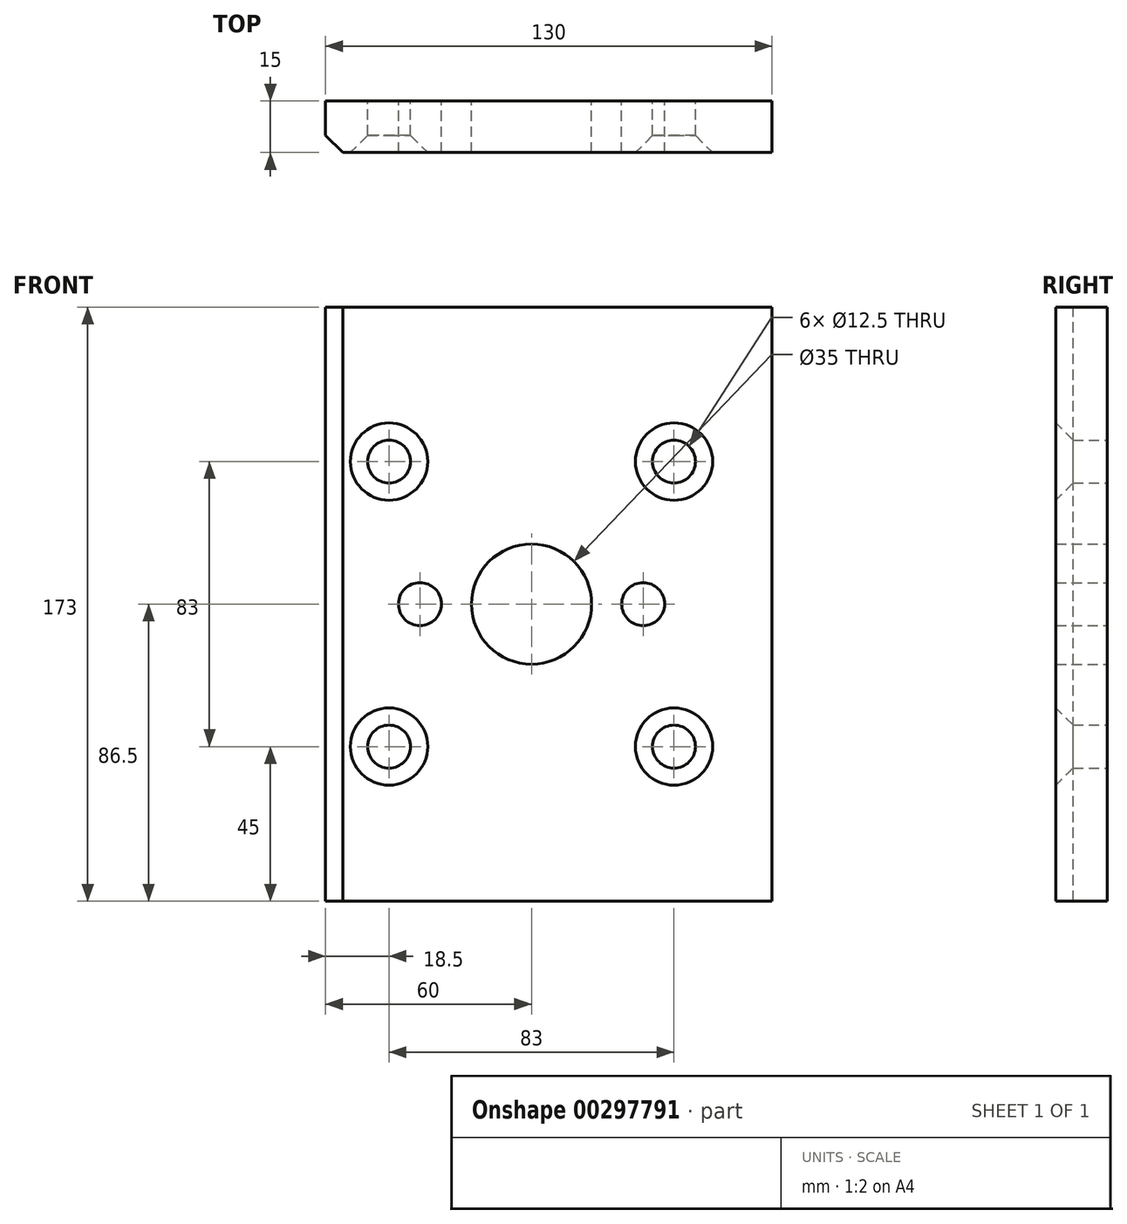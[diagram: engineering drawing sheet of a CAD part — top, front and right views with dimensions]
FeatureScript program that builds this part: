
annotation { "Feature Type Name" : "Feature", "Feature Type Description" : "" }
export const myFeature = defineFeature(function(context is Context, id is Id, definition is map)
    precondition{}
    {
        {
            var Q0;
            Q0=qCreatedBy(makeId("Front.planeOp"),FACE);
            var sketch = newSketch(context, id + "F0", { "sketchPlane" : qUnion([Q0])});
            skLineSegment(sketch, "E0.bottom", {"start": v(70, 86.5) * mm, "end": v(-60, 86.5) * mm});
            skLineSegment(sketch, "E0.top", {"start": v(70, -86.5) * mm, "end": v(-60, -86.5) * mm});
            skLineSegment(sketch, "E0.left", {"start": v(70, 86.5) * mm, "end": v(70, -86.5) * mm});
            skLineSegment(sketch, "E0.right", {"start": v(-60, 86.5) * mm, "end": v(-60, -86.5) * mm});
            skPoint(sketch, "E0.middle", {"position": v(0, 0) * mm});
            skCircle(sketch, "E1", {"center": v(0, 0) * mm, "radius": 17.5 * mm});
            skCircle(sketch, "E2", {"center": v(0, 0) * mm, "radius": 32.5 * mm, "construction": true});
            skCircle(sketch, "E3", {"center": v(-32.5, 0) * mm, "radius": 6.25 * mm});
            skCircle(sketch, "E4", {"center": v(32.5, 0) * mm, "radius": 6.25 * mm});
            skLineSegment(sketch, "E5.bottom", {"start": v(41.5, 41.5) * mm, "end": v(-41.5, 41.5) * mm, "construction": true});
            skLineSegment(sketch, "E5.top", {"start": v(41.5, -41.5) * mm, "end": v(-41.5, -41.5) * mm, "construction": true});
            skLineSegment(sketch, "E5.left", {"start": v(41.5, 41.5) * mm, "end": v(41.5, -41.5) * mm, "construction": true});
            skLineSegment(sketch, "E5.right", {"start": v(-41.5, 41.5) * mm, "end": v(-41.5, -41.5) * mm, "construction": true});
            skCircle(sketch, "E6", {"center": v(-41.5, 41.5) * mm, "radius": 6.25 * mm});
            skCircle(sketch, "E7", {"center": v(41.5, 41.5) * mm, "radius": 6.25 * mm});
            skCircle(sketch, "E8", {"center": v(41.5, -41.5) * mm, "radius": 6.25 * mm});
            skCircle(sketch, "E9", {"center": v(-41.5, -41.5) * mm, "radius": 6.25 * mm});
            skSolve(sketch);
        }
        {
            var Q0;
            Q0=qSketchRegion(id+"F0",true);
            extrude(context, id + "F1", {"entities" : qUnion([Q0]), "depth" : 15 * mm});
        }
        {
            var Q0;
            Q0=makeQuery(id+"F1.opExtrude","CAP_EDGE",EDGE,{"disambiguationData":[OSD([sQuery(id+"F0.wireOp",EDGE,"E6")])],"isStart":false});
            var Q1;
            Q1=makeQuery(id+"F1.opExtrude","CAP_EDGE",EDGE,{"disambiguationData":[OSD([sQuery(id+"F0.wireOp",EDGE,"E7")])],"isStart":false});
            var Q2;
            Q2=makeQuery(id+"F1.opExtrude","CAP_EDGE",EDGE,{"disambiguationData":[OSD([sQuery(id+"F0.wireOp",EDGE,"E9")])],"isStart":false});
            var Q3;
            Q3=makeQuery(id+"F1.opExtrude","CAP_EDGE",EDGE,{"disambiguationData":[OSD([sQuery(id+"F0.wireOp",EDGE,"E8")])],"isStart":false});
            var Q4;
            Q4=makeQuery(id+"F1.opExtrude","CAP_EDGE",EDGE,{"disambiguationData":[OSD([sQuery(id+"F0.wireOp",EDGE,"E0.right")])],"isStart":false});
            chamfer(context, id + "F2", {"entities" : qUnion([Q0, Q1, Q2, Q3, Q4]), "chamferType" : ChamferType.OFFSET_ANGLE, "width" : 5 * mm, "oppositeDirection" : false, "angle" : 45 * degree, "tangentPropagation" : true});
        }
    });
